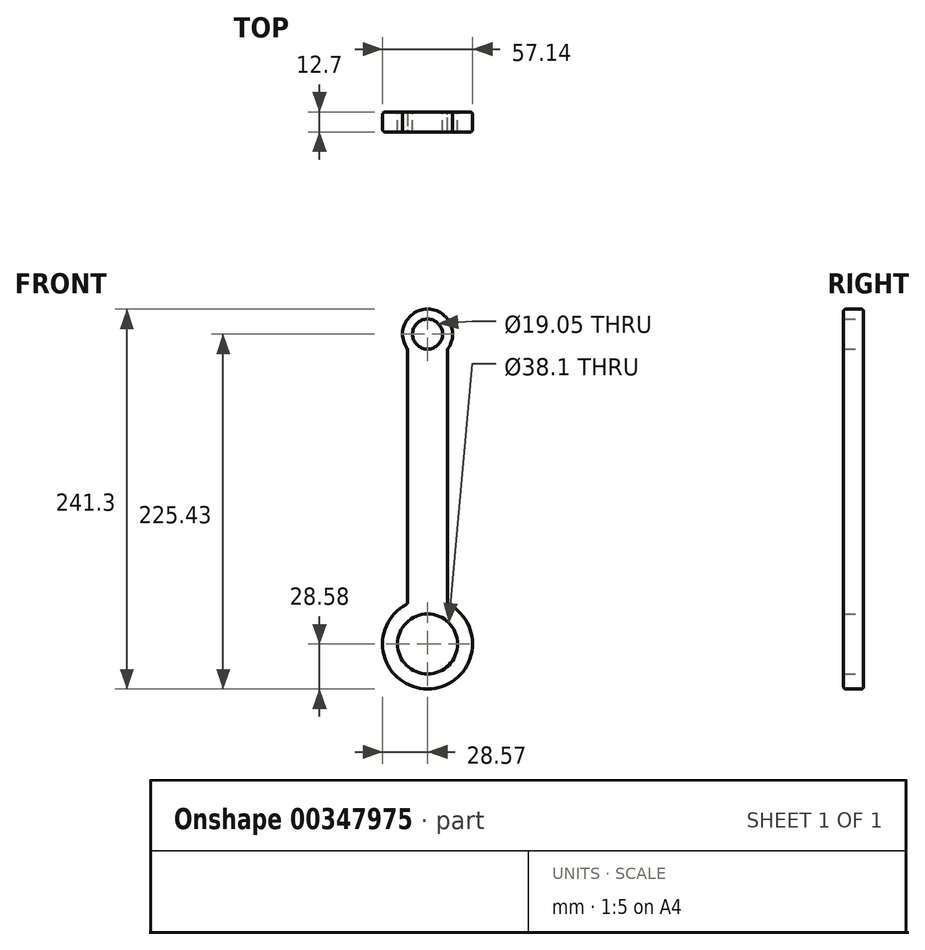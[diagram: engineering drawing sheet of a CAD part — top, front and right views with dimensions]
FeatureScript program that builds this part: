
annotation { "Feature Type Name" : "Feature", "Feature Type Description" : "" }
export const myFeature = defineFeature(function(context is Context, id is Id, definition is map)
    precondition{}
    {
        {
            var Q0;
            Q0=qCreatedBy(makeId("Front.planeOp"),FACE);
            var sketch = newSketch(context, id + "F0", { "sketchPlane" : qUnion([Q0])});
            skArc(sketch, "E0", {"start": v(-12.7, 25.6) * mm, "mid": v(0, -28.57) * mm, "end": v(12.7, 25.6) * mm});
            skCircle(sketch, "E1", {"center": v(0, 196.85) * mm, "radius": 9.53 * mm});
            skArc(sketch, "E2", {"start": v(12.7, 187.32) * mm, "mid": v(0, 212.73) * mm, "end": v(-12.7, 187.33) * mm});
            skLineSegment(sketch, "E3.bottom", {"start": v(12.7, 187.32) * mm, "end": v(12.7, 187.32) * mm});
            skLineSegment(sketch, "E3.left", {"start": v(-12.7, 187.33) * mm, "end": v(-12.7, 25.6) * mm});
            skLineSegment(sketch, "E3.right", {"start": v(12.7, 187.32) * mm, "end": v(12.7, 25.6) * mm});
            skCircle(sketch, "E4", {"center": v(0, 0) * mm, "radius": 19.05 * mm});
            skSolve(sketch);
        }
        {
            var Q0;
            Q0 = qSketchRegion(id + "F0", true);
            extrude(context, id + "F1", {"entities" : qUnion([Q0]), "depth" : 12.7 * mm});
        }
        {
            var Q0;
            Q0=makeQuery(id+"F1.opExtrude","CAP_EDGE",EDGE,{"disambiguationData":[OSD([sQuery(id+"F0.wireOp",EDGE,"E2")])],"isStart":false});
            var Q1;
            Q1=makeQuery(id+"F1.opExtrude","CAP_EDGE",EDGE,{"disambiguationData":[OSD([sQuery(id+"F0.wireOp",EDGE,"E3.right")])],"isStart":false});
            var Q2;
            Q2=makeQuery(id+"F1.opExtrude","CAP_EDGE",EDGE,{"disambiguationData":[OSD([sQuery(id+"F0.wireOp",EDGE,"E0")])],"isStart":false});
            var Q3;
            Q3=makeQuery(id+"F1.opExtrude","CAP_EDGE",EDGE,{"disambiguationData":[OSD([sQuery(id+"F0.wireOp",EDGE,"E3.left")])],"isStart":false});
            var Q4;
            Q4=makeQuery(id+"F1.opExtrude","CAP_EDGE",EDGE,{"disambiguationData":[OSD([sQuery(id+"F0.wireOp",EDGE,"E3.right")])],"isStart":true});
            var Q5;
            Q5=makeQuery(id+"F1.opExtrude","CAP_EDGE",EDGE,{"disambiguationData":[OSD([sQuery(id+"F0.wireOp",EDGE,"E2")])],"isStart":true});
            var Q6;
            Q6=makeQuery(id+"F1.opExtrude","CAP_EDGE",EDGE,{"disambiguationData":[OSD([sQuery(id+"F0.wireOp",EDGE,"E3.left")])],"isStart":true});
            var Q7;
            Q7=makeQuery(id+"F1.opExtrude","CAP_EDGE",EDGE,{"disambiguationData":[OSD([sQuery(id+"F0.wireOp",EDGE,"E0")])],"isStart":true});
            var Q8;
            Q8=makeQuery(id+"F1.opExtrude","SWEPT_EDGE",EDGE,{"disambiguationData":[OSD([sQuery(id+"F0.wireOp",EDGE,"E0"),sQuery(id+"F0.wireOp",EDGE,"E3.right")])]});
            var Q9;
            Q9=makeQuery(id+"F1.opExtrude","SWEPT_EDGE",EDGE,{"disambiguationData":[OSD([sQuery(id+"F0.wireOp",EDGE,"E2"),sQuery(id+"F0.wireOp",EDGE,"E3.right")])]});
            var Q10;
            Q10=makeQuery(id+"F1.opExtrude","SWEPT_EDGE",EDGE,{"disambiguationData":[OSD([sQuery(id+"F0.wireOp",EDGE,"E2"),sQuery(id+"F0.wireOp",EDGE,"E3.left")])]});
            var Q11;
            Q11=makeQuery(id+"F1.opExtrude","SWEPT_EDGE",EDGE,{"disambiguationData":[OSD([sQuery(id+"F0.wireOp",EDGE,"E0"),sQuery(id+"F0.wireOp",EDGE,"E3.left")])]});
            fillet(context, id + "F2", {"entities" : qUnion([Q0, Q1, Q2, Q3, Q4, Q5, Q6, Q7, Q8, Q9, Q10, Q11]), "radius" : 1.6 * mm, "tangentPropagation" : true, "allowEdgeOverflow" : false});
        }
    });
